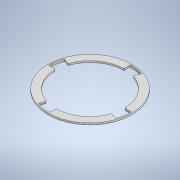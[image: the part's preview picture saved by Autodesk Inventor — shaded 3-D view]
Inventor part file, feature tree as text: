
AUTODESK INVENTOR PART (.ipt)
format: ipt  version: 2020 (Build 240168000, 168)  size: 279,040 bytes
history: native  units: mm
features: fillet x3, extrude x2, sketch x1
ambient origin geometry x8: Origin, YZ Plane, XZ Plane, XY Plane, X Axis, Y Axis, Z Axis, Center Point
bodies: Solid1 (feature_tree)
feature tree (6):
  extrude  "Extrusion1"  Depth=0.5mm
  fillet  "Fillet7"  Radius=58.0mm
  extrude  "Extrusion5"  Depth=0.5mm
  fillet  "Fillet11"  Radius=12.496557mm
  fillet  "Fillet12"  Radius=0.122173mm
  sketch  "Sketch5"  dims[d0=70.0mm d1=68.0mm d2=58.0mm d4=15.830136mm d5=12.496557mm d6=0.122173mm d7=3.211406mm d8=15.58579mm d9=18.919369mm d10=31.293753mm d11=28.204521mm d12=2.0mm d13=0.0mm d21=0.6mm d32=0.7mm d40=2.0mm d42=2.0mm d44=2.0mm d46=2.0mm d53=57.1mm d54=58.0mm d55=2.0mm d56=0.0mm d57=0.7mm d58=0.5mm]
